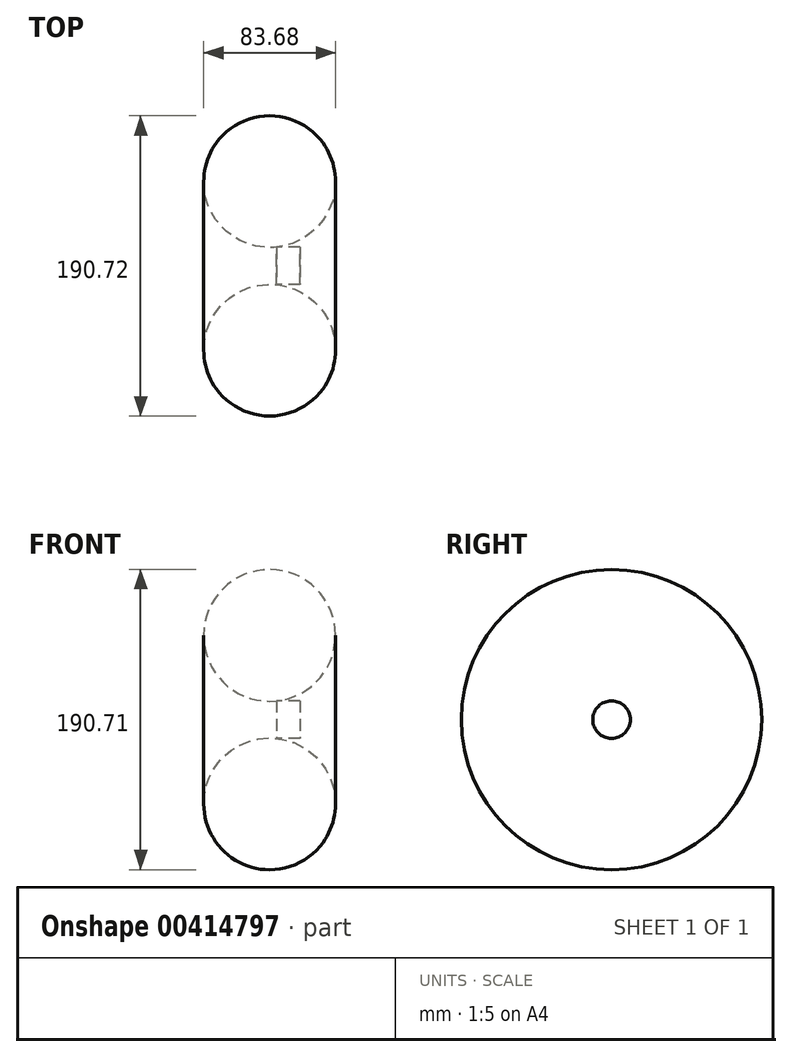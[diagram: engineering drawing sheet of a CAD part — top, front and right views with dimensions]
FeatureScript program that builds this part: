
annotation { "Feature Type Name" : "Feature", "Feature Type Description" : "" }
export const myFeature = defineFeature(function(context is Context, id is Id, definition is map)
    precondition{}
    {
        {
            var Q0;
            Q0=qCreatedBy(makeId("Front.planeOp"),FACE);
            var sketch = newSketch(context, id + "F0", { "sketchPlane" : qUnion([Q0])});
            skCircle(sketch, "E0", {"center": v(0, 0) * mm, "radius": 41.84 * mm});
            skLineSegment(sketch, "E1.bottom", {"start": v(4.46, 41.6) * mm, "end": v(19.4, 41.6) * mm});
            skLineSegment(sketch, "E1.top", {"start": v(4.46, 53.52) * mm, "end": v(19.4, 53.52) * mm});
            skLineSegment(sketch, "E1.left", {"start": v(4.46, 41.6) * mm, "end": v(4.46, 53.52) * mm});
            skLineSegment(sketch, "E1.right", {"start": v(19.4, 41.6) * mm, "end": v(19.4, 53.52) * mm});
            skLineSegment(sketch, "E2.bottom", {"start": v(-99.64, -37.03) * mm, "end": v(-103.83, -37.03) * mm});
            skLineSegment(sketch, "E2.top", {"start": v(-99.64, -46.34) * mm, "end": v(-103.83, -46.34) * mm});
            skLineSegment(sketch, "E2.left", {"start": v(-99.64, -37.03) * mm, "end": v(-99.64, -46.34) * mm});
            skLineSegment(sketch, "E2.right", {"start": v(-103.83, -37.03) * mm, "end": v(-103.83, -46.34) * mm});
            skSolve(sketch);
        }
        {
            var Q0;
            Q0=makeQuery(id+"F0.imprint","IMPRINT",FACE,{"disambiguationData":[TD([[makeQuery(id+"F0.imprint","IMPRINT",EDGE,{"derivedFrom":sQuery(id+"F0.wireOp",EDGE,"E1.bottom")}),1.0]])]});
            var Q1;
            Q1=makeQuery(id+"F0.imprint","IMPRINT",FACE,{"disambiguationData":[TD([[makeQuery(id+"F0.imprint","IMPRINT",EDGE,{"derivedFrom":sQuery(id+"F0.wireOp",EDGE,"E0")}),1.0]])]});
            var Q2;
            Q2=sQuery(id+"F0.wireOp",EDGE,"E1.top");
            revolve(context, id + "F1", {"entities" : qUnion([Q0, Q1]), "axis" : qUnion([Q2]), "revolveType" : RevolveType.FULL});
        }
    });
